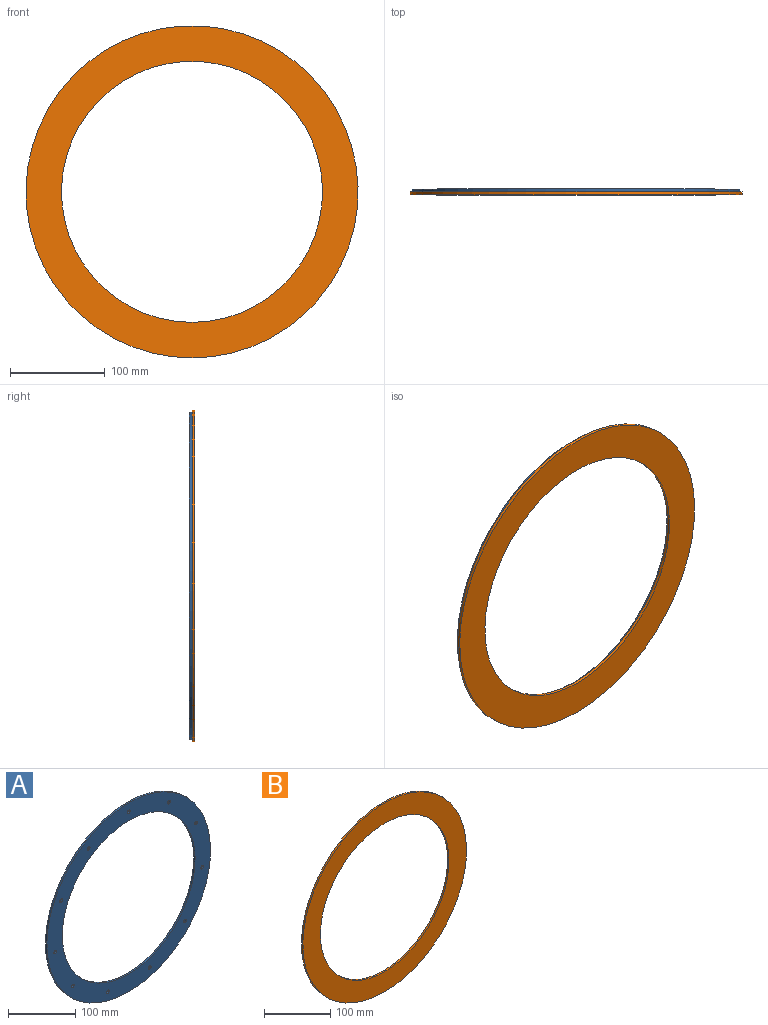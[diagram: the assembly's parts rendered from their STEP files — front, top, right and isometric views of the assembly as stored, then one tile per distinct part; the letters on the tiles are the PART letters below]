
ASSEMBLY  parts=2 mates=1
PART A: 15 faces, bbox 345x3x345 mm
  f0: cylinder r=140mm len=280mm, axis (0,1,0), area 2638.9mm2, adj f2,f3
  f1: cylinder r=172.5mm len=345mm, axis (0,1,0), area 3251.5mm2, adj f2,f3
  f2: plane 345x345mm, normal (0,-1,0), area 31595.8mm2, adj f0,f1,f4,f5,f6,f7,f8,f9
  f3: plane 345x345mm, normal (0,1,0), area 31595.8mm2, adj f0,f1,f4,f5,f6,f7,f8,f9
  f4: cylinder r=3mm len=6mm, axis (0,-1,0), area 56.5mm2, adj f2,f3
  f5: cylinder r=3mm len=6mm, axis (0,-1,0), area 56.5mm2, adj f2,f3
  f6: cylinder r=3mm len=6mm, axis (0,-1,0), area 56.5mm2, adj f2,f3
  f7: cylinder r=3mm len=6mm, axis (0,-1,0), area 56.5mm2, adj f2,f3
  f8: cylinder r=3mm len=6mm, axis (0,-1,0), area 56.5mm2, adj f2,f3
  f9: cylinder r=3mm len=6mm, axis (0,-1,0), area 56.5mm2, adj f2,f3
  f10: cylinder r=3mm len=6mm, axis (0,-1,0), area 56.5mm2, adj f2,f3
  f11: cylinder r=3mm len=6mm, axis (0,-1,0), area 56.5mm2, adj f2,f3
  f12: cylinder r=3mm len=6mm, axis (0,-1,0), area 56.5mm2, adj f2,f3
  f13: cylinder r=3mm len=6mm, axis (0,-1,0), area 56.5mm2, adj f2,f3
  f14: cylinder r=3mm len=6mm, axis (0,-1,0), area 56.5mm2, adj f2,f3
PART B: 4 faces, bbox 350x3x350 mm
  f0: cylinder r=137.5mm len=275mm, axis (0,1,0), area 2591.8mm2, adj f2,f3
  f1: cylinder r=175mm len=350mm, axis (0,1,0), area 3298.7mm2, adj f2,f3
  f2: plane 350x350mm, normal (0,-1,0), area 36815.5mm2, adj f0,f1
  f3: plane 350x350mm, normal (0,1,0), area 36815.5mm2, adj f0,f1
PLACE A t=(-169.89,-96.28,25.06)mm
PLACE B t=(-169.89,-99.28,25.06)mm
MATE fastened B.f1 <-> A.f1  axis (0,1,0) through (-169.89,-99.28,25.06)mm
